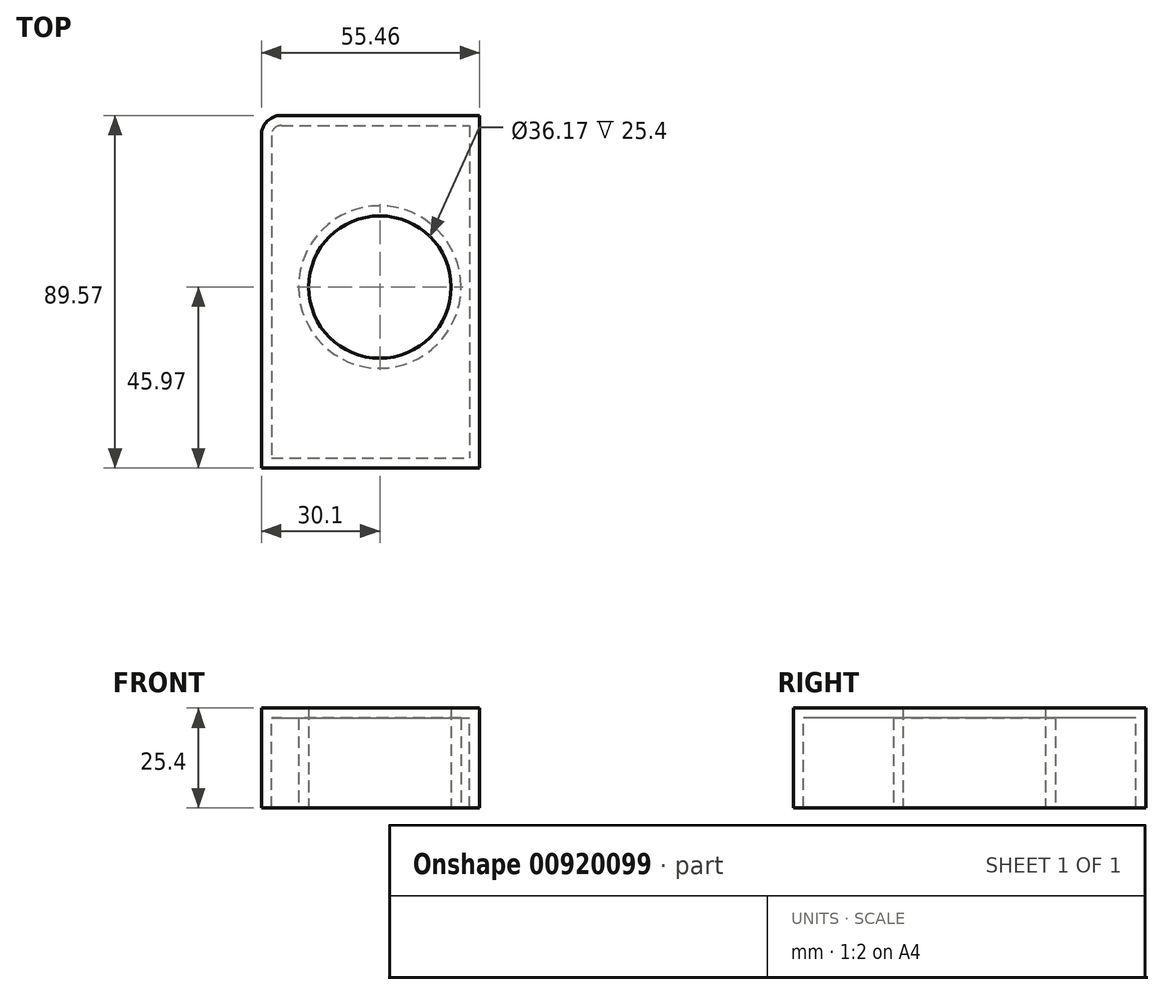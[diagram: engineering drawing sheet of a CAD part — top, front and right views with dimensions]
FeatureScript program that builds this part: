
annotation { "Feature Type Name" : "Feature", "Feature Type Description" : "" }
export const myFeature = defineFeature(function(context is Context, id is Id, definition is map)
    precondition{}
    {
        {
            var Q0;
            Q0=qCreatedBy(makeId("Top.planeOp"),FACE);
            var sketch = newSketch(context, id + "F0", { "sketchPlane" : qUnion([Q0])});
            skLineSegment(sketch, "E0.bottom", {"start": v(-30.1, 43.6) * mm, "end": v(25.36, 43.6) * mm});
            skLineSegment(sketch, "E0.top", {"start": v(-30.1, -45.97) * mm, "end": v(25.36, -45.97) * mm});
            skLineSegment(sketch, "E0.left", {"start": v(-30.1, 43.6) * mm, "end": v(-30.1, -45.97) * mm});
            skLineSegment(sketch, "E0.right", {"start": v(25.36, 43.6) * mm, "end": v(25.36, -45.97) * mm});
            skSolve(sketch);
        }
        {
            var Q0;
            Q0 = qSketchRegion(id + "F0", true);
            extrude(context, id + "F1", {"entities" : qUnion([Q0]), "oppositeDirection" : true, "depth" : 25.4 * mm, "offsetDistance" : 25.4 * mm});
        }
        {
            var Q0;
            Q0=makeQuery(id+"F1.opExtrude","SWEPT_EDGE",EDGE,{"disambiguationData":[OSD([sQuery(id+"F0.wireOp",EDGE,"E0.bottom"),sQuery(id+"F0.wireOp",EDGE,"E0.left")])]});
            fillet(context, id + "F2", {"entities" : qUnion([Q0]), "radius" : 5.08 * mm, "tangentPropagation" : true, "allowEdgeOverflow" : false});
        }
        {
            var Q0;
            Q0=makeQuery(id+"F1.opExtrude","CAP_FACE",FACE,{"disambiguationData":[OSD([sQuery(id+"F0.wireOp",EDGE,"E0.bottom"),sQuery(id+"F0.wireOp",EDGE,"E0.top"),sQuery(id+"F0.wireOp",EDGE,"E0.left"),sQuery(id+"F0.wireOp",EDGE,"E0.right")])],"isStart":false});
            var sketch = newSketch(context, id + "F3", { "sketchPlane" : qUnion([Q0])});
            skCircle(sketch, "E1", {"center": v(0, 0) * mm, "radius": 18.09 * mm});
            skSolve(sketch);
        }
        {
            var Q0;
            Q0 = qSketchRegion(id + "F3", true);
            extrude(context, id + "F4", {"entities" : qUnion([Q0]), "operationType" : NewBodyOperationType.REMOVE, "oppositeDirection" : true, "depth" : 25.4 * mm, "offsetDistance" : 25.4 * mm});
        }
        {
            var Q0;
            Q0=makeQuery(id+"F1.opExtrude","CAP_FACE",FACE,{"disambiguationData":[OSD([sQuery(id+"F0.wireOp",EDGE,"E0.bottom"),sQuery(id+"F0.wireOp",EDGE,"E0.top"),sQuery(id+"F0.wireOp",EDGE,"E0.left"),sQuery(id+"F0.wireOp",EDGE,"E0.right")])],"isStart":false});
            shell(context, id + "F5", {"entities" : qUnion([Q0]), "thickness" : 2.54 * mm});
        }
    });
